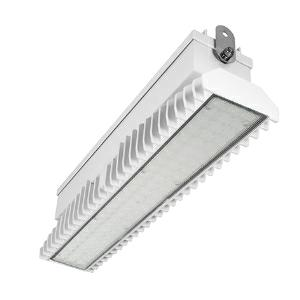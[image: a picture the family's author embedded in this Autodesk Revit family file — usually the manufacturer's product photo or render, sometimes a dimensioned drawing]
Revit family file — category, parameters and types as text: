
# Revit family: 3f_filippi_-_3f_lem_ho_concentrato_3f_filippi_-_58959_a0812_-_3f_lem_1_ho_led_70_cr_conc___vs_3aaa
name_source: partatom
category: Lighting Fixtures
units: mm (PartAtom-declared; Revit-internal decimal feet)

## family parameters
Cut with Voids When Loaded = No
Host = Face
Light Source = No
Part Type = Normal
Room Calculation Point = No
Round Connector Dimension = Use Diameter
Shared = No

## types (1)
- 3F Filippi - 3F LEM HO Concentrato (1 x LED, 8791 lm, 71 W, 4000 K)
    Apparent Load = 71 VA
    Approval mark = CE
    CIE Flux Codes = 78 93 98 100 100
    Color Rendering = 80
    Color Temperature = 4000 K
    Control Gear = Electronic ballast
    Default Elevation = 1800 mm
    Description = Industrial luminaire with high light output and high luminous efficiency designed with the most innovative technologies for environments with temperature up to 55°C.

ILLUMINOTECHNICAL
Luminous efficiency 100% (DLOR 98%, ULOR 2%).
Initial luminous flux of the luminaire 8791 lm.
Direct symmetric narrow distribution: the illuminated area has a elliptical shape.
Installation Interdistance Transv.D = 0.60 x hu - Long.D = 0.91 x hu.
Tabular UGR (CIE 117 - 4H-8H; S=0.25H; 70/50/20): RUG 24.3 - 25.5.
Beam angle: 38° - 61°.
Luminous efficacy 124 lm/W.
Lifetime (L93/B10): 30000 h. (tq+25°C)
Lifetime (L90/B10): 50000 h. (tq+25°C)
Lifetime (L85/B10): 80000 h. (tq+25°C)
Lifetime (L80/B10): 100000 h. (tq+25°C)
Lifetime (L85/B10): 50000 h. (tq+55°C)
Sudden decreased luminous flux after 50000 hours: 0% (C0).
Photobiological safety in compliance with IEC/TR 62778: RG0 risk exempt, (IEC 62471).
In compliance with IEC/EN 62722-2-1 - IEC/EN 62717 standards.

SOURCE
Mid-Power linear LED module 70W/840.
Energy efficiency class (UE 2019/2020 - UE 2019/2015): C.
CIE 13.3 Colour rendering index: CRI >80 (R9 <50%).
IES TM-30 Fidelity Index: Rf = 84 Rg = 95.
CCT nominal colour temperature 4000 K.
Colour initial tolerance (MacAdam): SDCM 3.

MECHANICAL
Passive modular heatsinks in die-casted aluminium, painted in white colour.
To optimize the thermal management of the LED module, the heatsinks are oversized and provided with self-cleaning of cooling fins.
Wiring body in aluminium and galvanised steel anchored solidly to the sinks and thermally separated.
3F Lens lenses with high luminous efficiency, transparent methacrylate (PMMA), fixed to the LED modules.
Fixing brackets in stainless steel.
Luminaire with limited surface temperature. - D - (EN 60598-2-24)
Dimensions: 542x115 mm, height 154 mm. Weight 6.36 kg.
IP65 protection degree.
Mechanical strength to impacts IK06 (1 joule).
Glow-wire test resistance 650°C.

ELECTRICAL
Halogen Free electronic wiring 230V-50/60Hz, power factor 0.97, THD <25%, constant output current, class I, 1 driver.
Power of the luminaire 71 W.
ENEC - CE.
SAFE FLICKER: PstLM=<1 and SVM=<0.4 (IEC TR 61547-1 and IEC TR 63158), to ensure a more comfortable and safe light.
Luminaire compliant with EN 60598-2-22 for power supply from a centralised emergency system CPSS (Central Power Supply System), not incorporated in the luminaire - high risk areas excluded. The default power and flux are 100% in AC and 100% in DC.
Ambient temperature from -30°C to +55°C.
Temperature class T6 max 85°C.
Quick connection via M20 3P connector with 9-13 mm tightening range.
Power unit positioned on a separate compartment by the LED module to ensure optimum temperatures of cabling components, to be inspectable and maintainable.
Relative humidity UR: <85%.

INSTALLATION
Ceiling / Suspended / Wall.
All accessories dedicated to this product are available on the Catalog and on our website www.3F-Filippi.com.

ACCESSORIES
A0812 - Anti-glare microprismatic VS moulded glass, tempered, not flammable, with sealing gasket.
One required for each light module. The pack contains 10 pieces.

APPLICATIONS
In commercial environments, exhibition and industrial areas, stores, open areas or with shelves.
Environments in which it is necessary a total protection against falling fragments (eg environments with foodstuffs or machines with moving parts or with extreme temperature changes), use luminaires with polycarbonate lenses.

WARNING
Fixture not suitable for cold stores with an ambient temperature <0°C and/or relative humidity >85%.
Luminaire designed for disposal/recycling at end-of-life.
Replaceable (LED only) light source by a professional. Replaceable control gear by a professional.
    Height = 154 mm
    Lamp = 1 x LED
    Lamp Light Flux = 8791 lm
    Lamp Power = 71 W
    Lamp count = 1
    Length = 542 mm
    Lifetime = 50000 h
    Luminous efficacy = 124 lm/W
    Manufacturer = 3F Filippi
    ModVariant = No
    Model = 3F Filippi - 58959+A0812 - 3F LEM 1 HO LED 70 CR CONC + VS
    Mounting Place = Ceiling
    Mounting Type = Pendant
    Number of Poles = 1
    OnlyDefault = Yes
    Power Factor = 1
    Product Name = 3F Filippi - 3F LEM HO Concentrato
    Product group = pendant luminaire
    ProductGroupID = 9
    Protection Class = Protection class I
    Protection Degree = IP 65
    RLX_Detail_Level = 1
    RLX_Emergency_Light_Flux = 0 lm
    RLX_Emergency_Type = 0
    RLX_Emergency_Type_DB = No
    RlxData = <blob elided: 90761 chars, md5=fde6399b>
    Socket = socket
    Standby Power = 0 W
    System Light Flux = 8791 lm
    System Power = 71 W
    Type Comments = Product without accessories
    Type Image = 3f_filippi_-_lem_1__a0812.jpg
    URL = http://relux.com
    VarID = ---
    Voltage = 0 V
    Weight = 0.00 kg
    Width = 115 mm

## geometry (parser evidence)
native form markers: Blend x4, Sweep x13
no freeform markers — native parametric forms only
